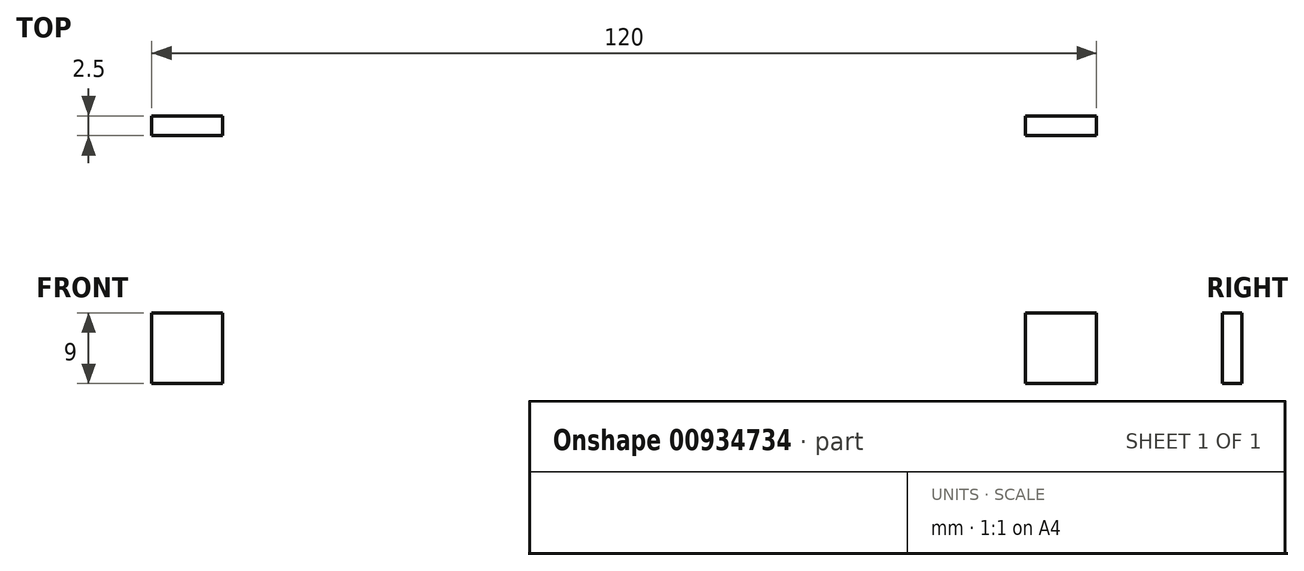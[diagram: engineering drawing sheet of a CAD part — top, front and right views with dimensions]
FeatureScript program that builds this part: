
annotation { "Feature Type Name" : "Feature", "Feature Type Description" : "" }
export const myFeature = defineFeature(function(context is Context, id is Id, definition is map)
    precondition{}
    {
        {
            var Q0;
            Q0=qCreatedBy(makeId("Front.planeOp"),FACE);
            var sketch = newSketch(context, id + "F0", { "sketchPlane" : qUnion([Q0])});
            skLineSegment(sketch, "E0.bottom", {"start": v(-60, 30) * mm, "end": v(60, 30) * mm});
            skLineSegment(sketch, "E0.top", {"start": v(-60, -30) * mm, "end": v(60, -30) * mm});
            skLineSegment(sketch, "E0.left", {"start": v(-60, 30) * mm, "end": v(-60, -30) * mm});
            skLineSegment(sketch, "E0.right", {"start": v(60, 30) * mm, "end": v(60, -30) * mm});
            skPoint(sketch, "E0.middle", {"position": v(0, 0) * mm});
            skLineSegment(sketch, "E1.bottom", {"start": v(-60, 30) * mm, "end": v(-51, 30) * mm});
            skLineSegment(sketch, "E1.top", {"start": v(-60, 21) * mm, "end": v(-51, 21) * mm});
            skLineSegment(sketch, "E1.left", {"start": v(-60, 30) * mm, "end": v(-60, 21) * mm});
            skLineSegment(sketch, "E1.right", {"start": v(-51, 30) * mm, "end": v(-51, 21) * mm});
            skLineSegment(sketch, "E2.bottom", {"start": v(51, 30) * mm, "end": v(60, 30) * mm});
            skLineSegment(sketch, "E2.top", {"start": v(51, 21) * mm, "end": v(60, 21) * mm});
            skLineSegment(sketch, "E2.left", {"start": v(51, 30) * mm, "end": v(51, 21) * mm});
            skLineSegment(sketch, "E2.right", {"start": v(60, 30) * mm, "end": v(60, 21) * mm});
            skLineSegment(sketch, "E3.bottom", {"start": v(-60, -30) * mm, "end": v(-51, -30) * mm});
            skLineSegment(sketch, "E3.top", {"start": v(-60, -21) * mm, "end": v(-51, -21) * mm});
            skLineSegment(sketch, "E3.left", {"start": v(-60, -30) * mm, "end": v(-60, -21) * mm});
            skLineSegment(sketch, "E3.right", {"start": v(-51, -30) * mm, "end": v(-51, -21) * mm});
            skLineSegment(sketch, "E4.bottom", {"start": v(60, -30) * mm, "end": v(51, -30) * mm});
            skLineSegment(sketch, "E4.top", {"start": v(60, -21) * mm, "end": v(51, -21) * mm});
            skLineSegment(sketch, "E4.left", {"start": v(60, -30) * mm, "end": v(60, -21) * mm});
            skLineSegment(sketch, "E4.right", {"start": v(51, -30) * mm, "end": v(51, -21) * mm});
            skSolve(sketch);
        }
        {
            var Q0;
            Q0=makeQuery(id+"F0.imprint","IMPRINT",FACE,{"disambiguationData":[TD([[makeQuery(id+"F0.imprint","IMPRINT",EDGE,{"derivedFrom":sQuery(id+"F0.wireOp",EDGE,"E0.bottom")}),-1.0]])]});
            extrude(context, id + "F1", {"entities" : qUnion([Q0]), "depth" : 2.5 * mm, "offsetDistance" : 25 * mm});
        }
    });
